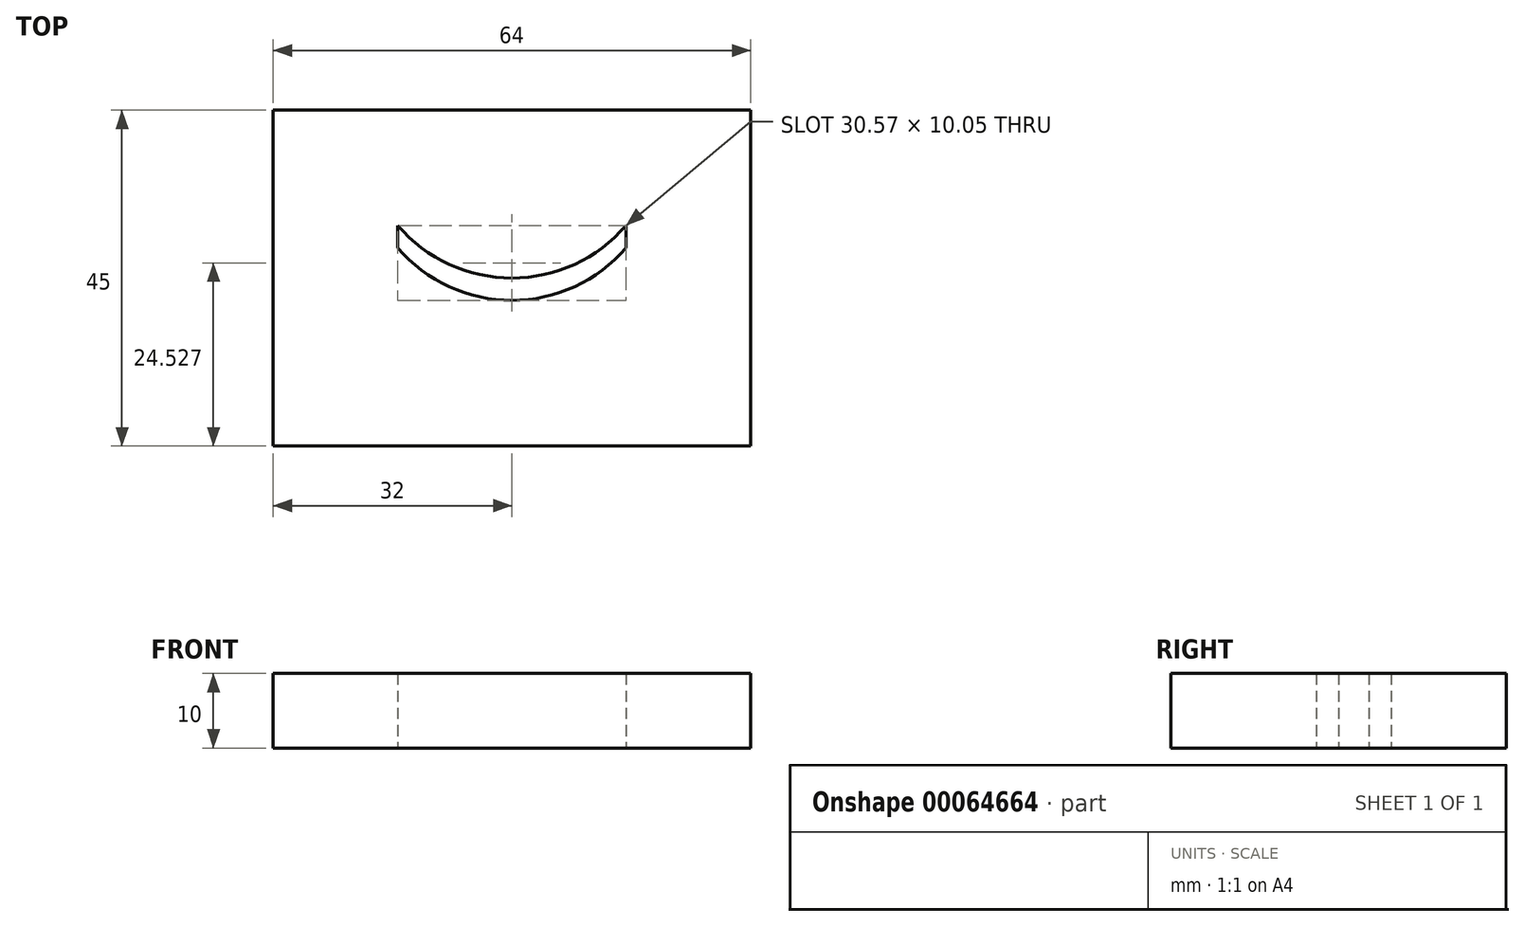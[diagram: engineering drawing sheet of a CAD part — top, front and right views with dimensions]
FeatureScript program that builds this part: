
annotation { "Feature Type Name" : "Feature", "Feature Type Description" : "" }
export const myFeature = defineFeature(function(context is Context, id is Id, definition is map)
    precondition{}
    {
        {
            var Q0;
            Q0=qCreatedBy(makeId("Top.planeOp"),FACE);
            var sketch = newSketch(context, id + "F0", { "sketchPlane" : qUnion([Q0])});
            skLineSegment(sketch, "E0.rect.bottom", {"start": v(-32, -22.5) * mm, "end": v(32, -22.5) * mm});
            skLineSegment(sketch, "E0.rect.top", {"start": v(-32, 22.5) * mm, "end": v(32, 22.5) * mm});
            skLineSegment(sketch, "E0.rect.left", {"start": v(-32, -22.5) * mm, "end": v(-32, 22.5) * mm});
            skLineSegment(sketch, "E0.rect.right", {"start": v(32, -22.5) * mm, "end": v(32, 22.5) * mm});
            skPoint(sketch, "E0.rect.middle", {"position": v(0, 0) * mm});
            skLineSegment(sketch, "E1", {"start": v(0, 0) * mm, "end": v(0, 6) * mm, "construction": true});
            skArc(sketch, "E2.0", {"start": v(-15.28, 4.05) * mm, "mid": v(0, -3) * mm, "end": v(15.28, 4.05) * mm});
            skLineSegment(sketch, "E3", {"start": v(-15.28, 4.05) * mm, "end": v(-15.28, 7.05) * mm});
            skLineSegment(sketch, "E4", {"start": v(15.28, 4.05) * mm, "end": v(15.28, 7.05) * mm});
            skArc(sketch, "E5", {"start": v(-15.28, 7.05) * mm, "mid": v(0, 0) * mm, "end": v(15.28, 7.05) * mm});
            skSolve(sketch);
        }
        {
            var Q0;
            Q0=makeQuery(id+"F0.imprint","IMPRINT",FACE,{"disambiguationData":[TD([[makeQuery(id+"F0.imprint","IMPRINT",EDGE,{"derivedFrom":sQuery(id+"F0.wireOp",EDGE,"E0.rect.bottom")}),1.0]])]});
            extrude(context, id + "F1", {"entities" : qUnion([Q0]), "depth" : 10 * mm});
        }
    });
